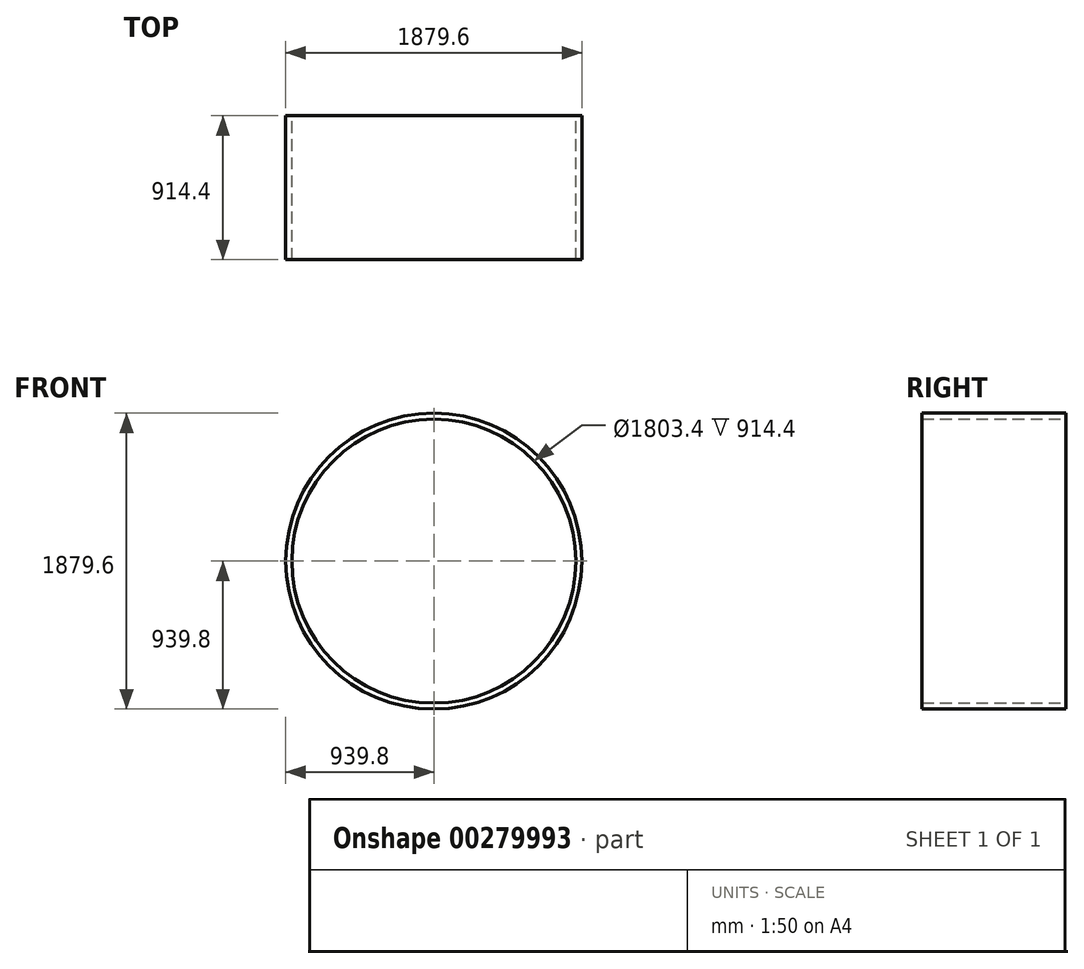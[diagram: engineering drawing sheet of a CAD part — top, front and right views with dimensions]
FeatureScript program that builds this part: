
annotation { "Feature Type Name" : "Feature", "Feature Type Description" : "" }
export const myFeature = defineFeature(function(context is Context, id is Id, definition is map)
    precondition{}
    {
        {
            var Q0;
            Q0=qCreatedBy(makeId("Front.planeOp"),FACE);
            var sketch = newSketch(context, id + "F0", { "sketchPlane" : qUnion([Q0])});
            skCircle(sketch, "E0", {"center": v(0, 0) * mm, "radius": 939.8 * mm});
            skCircle(sketch, "E1", {"center": v(0, 0) * mm, "radius": 901.7 * mm});
            skSolve(sketch);
        }
        {
            var Q0;
            Q0=makeQuery(id+"F0.imprint","IMPRINT",FACE,{"disambiguationData":[TD([[makeQuery(id+"F0.imprint","IMPRINT",EDGE,{"derivedFrom":sQuery(id+"F0.wireOp",EDGE,"E0")}),1.0]])]});
            extrude(context, id + "F1", {"entities" : qUnion([Q0]), "depth" : 914.4 * mm});
        }
    });
